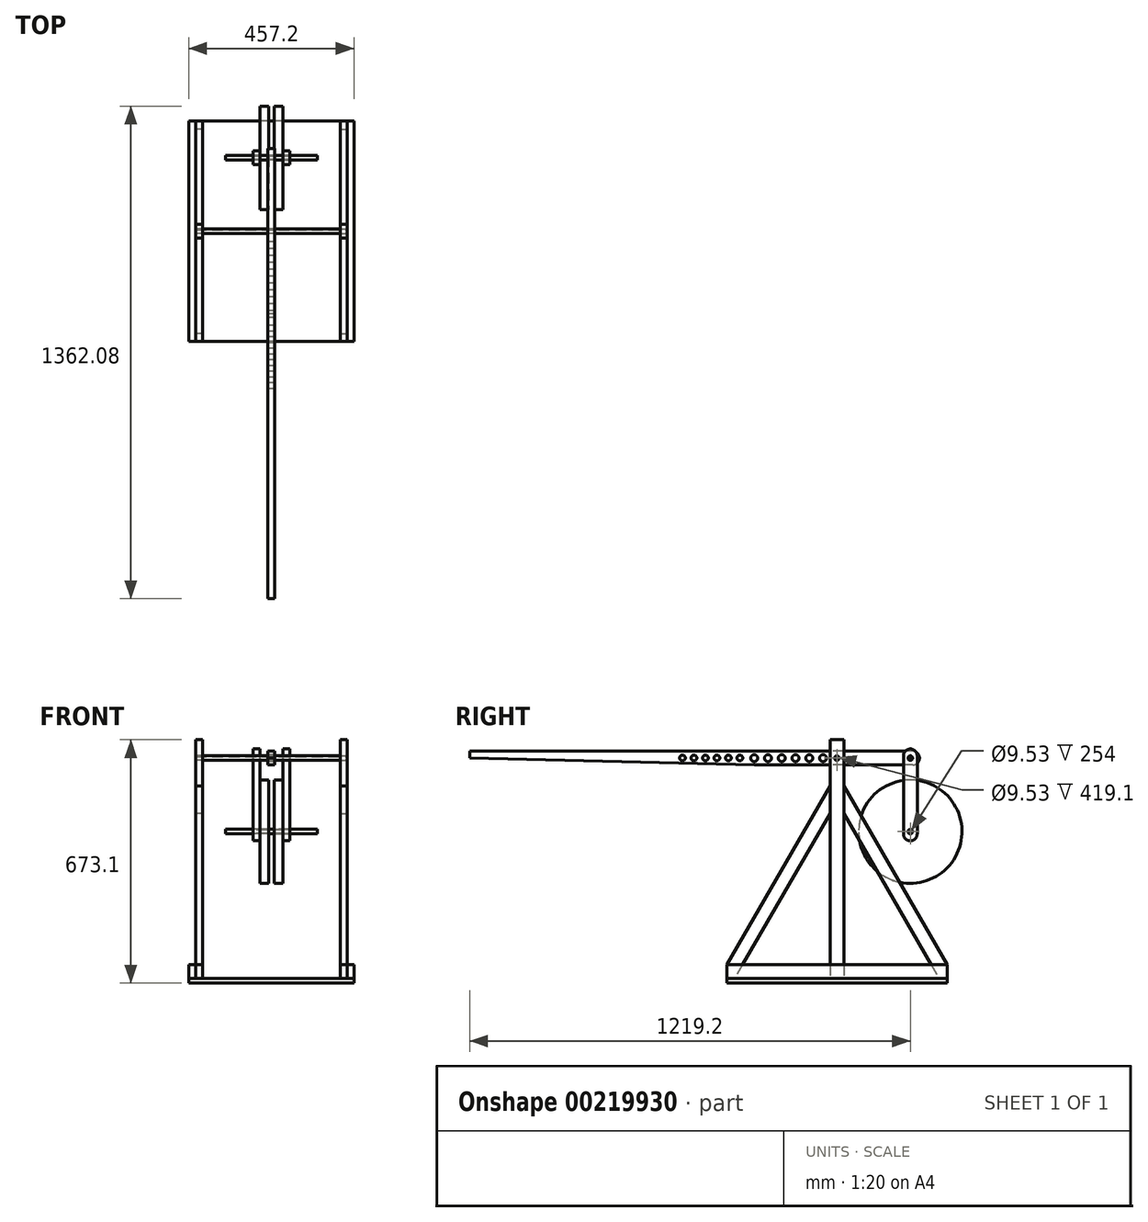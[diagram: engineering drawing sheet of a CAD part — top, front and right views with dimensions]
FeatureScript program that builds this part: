
annotation { "Feature Type Name" : "Feature", "Feature Type Description" : "" }
export const myFeature = defineFeature(function(context is Context, id is Id, definition is map)
    precondition{}
    {
        {
            var Q0;
            Q0=qCreatedBy(makeId("Top.planeOp"),FACE);
            var sketch = newSketch(context, id + "F0", { "sketchPlane" : qUnion([Q0])});
            skLineSegment(sketch, "E0.bottom", {"start": v(-228.6, -304.8) * mm, "end": v(228.6, -304.8) * mm, "construction": true});
            skLineSegment(sketch, "E0.top", {"start": v(-228.6, 304.8) * mm, "end": v(228.6, 304.8) * mm, "construction": true});
            skLineSegment(sketch, "E0.left", {"start": v(-228.6, -304.8) * mm, "end": v(-228.6, 304.8) * mm, "construction": true});
            skLineSegment(sketch, "E0.right", {"start": v(228.6, -304.8) * mm, "end": v(228.6, 304.8) * mm, "construction": true});
            skPoint(sketch, "E0.middle", {"position": v(0, 0) * mm});
            skLineSegment(sketch, "E1.bottom", {"start": v(-228.6, 304.8) * mm, "end": v(-209.55, 304.8) * mm});
            skLineSegment(sketch, "E1.top", {"start": v(-228.6, -304.8) * mm, "end": v(-209.55, -304.8) * mm});
            skLineSegment(sketch, "E1.left", {"start": v(-228.6, 304.8) * mm, "end": v(-228.6, -304.8) * mm});
            skLineSegment(sketch, "E1.right", {"start": v(-209.55, 304.8) * mm, "end": v(-209.55, -304.8) * mm});
            skLineSegment(sketch, "E2.MirrorCS", {"start": v(228.6, -304.8) * mm, "end": v(209.55, -304.8) * mm});
            skLineSegment(sketch, "E3.MirrorCS", {"start": v(228.6, 304.8) * mm, "end": v(228.6, -304.8) * mm});
            skLineSegment(sketch, "E4.MirrorCS", {"start": v(209.55, 304.8) * mm, "end": v(209.55, -304.8) * mm});
            skLineSegment(sketch, "E5.MirrorCS", {"start": v(228.6, 304.8) * mm, "end": v(209.55, 304.8) * mm});
            skSolve(sketch);
        }
        {
            var Q0;
            Q0=makeQuery(id+"F0.imprint","IMPRINT",FACE,{"disambiguationData":[TD([[makeQuery(id+"F0.imprint","IMPRINT",EDGE,{"derivedFrom":sQuery(id+"F0.wireOp",EDGE,"E1.bottom")}),-1.0]])]});
            var Q1;
            Q1=makeQuery(id+"F0.imprint","IMPRINT",FACE,{"disambiguationData":[TD([[makeQuery(id+"F0.imprint","IMPRINT",EDGE,{"derivedFrom":sQuery(id+"F0.wireOp",EDGE,"E2.MirrorCS")}),-1.0]])]});
            extrude(context, id + "F1", {"entities" : qUnion([Q0, Q1]), "depth" : 38.1 * mm});
        }
        {
            var Q0;
            Q0=makeQuery(id+"F1.opExtrude","SWEPT_FACE",FACE,{"disambiguationData":[OSD([sQuery(id+"F0.wireOp",EDGE,"E1.right")])]});
            var sketch = newSketch(context, id + "F2", { "sketchPlane" : qUnion([Q0])});
            skLineSegment(sketch, "E6", {"start": v(-304.8, 0) * mm, "end": v(-304.8, 38.1) * mm});
            skLineSegment(sketch, "E7", {"start": v(-304.8, 38.1) * mm, "end": v(-19.05, 533.03) * mm});
            skLineSegment(sketch, "E8", {"start": v(-19.05, 456.83) * mm, "end": v(-19.05, 533.03) * mm});
            skLineSegment(sketch, "E9", {"start": v(-19.05, 456.83) * mm, "end": v(-282.8, 0) * mm});
            skLineSegment(sketch, "E10", {"start": v(-282.8, 0) * mm, "end": v(-304.8, 0) * mm});
            skLineSegment(sketch, "E11.bottom", {"start": v(-19.05, 660.4) * mm, "end": v(19.05, 660.4) * mm});
            skLineSegment(sketch, "E11.top", {"start": v(-19.05, 0) * mm, "end": v(19.05, 0) * mm});
            skLineSegment(sketch, "E11.left", {"start": v(-19.05, 660.4) * mm, "end": v(-19.05, 0) * mm});
            skLineSegment(sketch, "E11.right", {"start": v(19.05, 660.4) * mm, "end": v(19.05, 0) * mm});
            skLineSegment(sketch, "E12.MirrorCS", {"start": v(304.8, 0) * mm, "end": v(304.8, 38.1) * mm});
            skLineSegment(sketch, "E13.MirrorCS", {"start": v(282.8, 0) * mm, "end": v(304.8, 0) * mm});
            skLineSegment(sketch, "E14.MirrorCS", {"start": v(19.05, 456.83) * mm, "end": v(282.8, 0) * mm});
            skLineSegment(sketch, "E15.MirrorCS", {"start": v(304.8, 38.1) * mm, "end": v(19.05, 533.03) * mm});
            skLineSegment(sketch, "E16.MirrorCS", {"start": v(19.05, 456.83) * mm, "end": v(19.05, 533.03) * mm});
            skCircle(sketch, "E17", {"center": v(0, 609.6) * mm, "radius": 6.35 * mm});
            skSolve(sketch);
        }
        {
            var Q0;
            {var subQ0=sQuery(id+"F2.wireOp",EDGE,"E7");Q0=makeQuery(id+"F2.imprint","IMPRINT",FACE,{"disambiguationData":[TD([[makeQuery(id+"F2.imprint","IMPRINT",EDGE,{"derivedFrom":subQ0}),-1.0]])]});}
            var Q1;
            {var subQ0=sQuery(id+"F2.wireOp",EDGE,"E6");Q1=makeQuery(id+"F2.imprint","IMPRINT",FACE,{"disambiguationData":[TD([[makeQuery(id+"F2.imprint","IMPRINT",EDGE,{"derivedFrom":subQ0}),1.0]])]});}
            var Q2;
            {var subQ4=sQuery(id+"F2.wireOp",EDGE,"E15.MirrorCS");Q2=makeQuery(id+"F2.imprint","IMPRINT",FACE,{"disambiguationData":[TD([[makeQuery(id+"F2.imprint","IMPRINT",EDGE,{"derivedFrom":subQ4}),1.0]])]});}
            var Q3;
            {var subQ0=sQuery(id+"F2.wireOp",EDGE,"E12.MirrorCS");Q3=makeQuery(id+"F2.imprint","IMPRINT",FACE,{"disambiguationData":[TD([[makeQuery(id+"F2.imprint","IMPRINT",EDGE,{"derivedFrom":subQ0}),-1.0]])]});}
            extrude(context, id + "F3", {"entities" : qUnion([Q0, Q1, Q2, Q3]), "depth" : 19.05 * mm});
        }
        {
            var Q0;
            {var subQ5=sQuery(id+"F2.wireOp",EDGE,"E11.bottom");Q0=makeQuery(id+"F2.imprint","IMPRINT",FACE,{"disambiguationData":[TD([[makeQuery(id+"F2.imprint","IMPRINT",EDGE,{"derivedFrom":subQ5}),-1.0]])]});}
            var Q1;
            {var subQ0=sQuery(id+"F2.wireOp",EDGE,"E11.top");Q1=makeQuery(id+"F2.imprint","IMPRINT",FACE,{"disambiguationData":[TD([[makeQuery(id+"F2.imprint","IMPRINT",EDGE,{"derivedFrom":subQ0}),-1.0]])]});}
            extrude(context, id + "F4", {"entities" : qUnion([Q0, Q1]), "depth" : 19.05 * mm});
        }
        {
            var Q0;
            Q0=makeQuery(id+"F3.opExtrude","SWEPT_BODY",BODY,{"disambiguationData":[OSD([sQuery(id+"F2.wireOp",EDGE,"E12.MirrorCS"),sQuery(id+"F2.wireOp",EDGE,"E13.MirrorCS"),sQuery(id+"F2.wireOp",EDGE,"E14.MirrorCS"),sQuery(id+"F2.wireOp",EDGE,"E15.MirrorCS"),sQuery(id+"F2.wireOp",EDGE,"E16.MirrorCS")])]});
            var Q1;
            Q1=qCreatedBy(makeId("Right.planeOp"),FACE);
            mirror(context, id + "F5", {"entities" : qUnion([Q0]), "mirrorPlane" : qUnion([Q1])});
        }
        {
            var Q0;
            Q0=makeQuery(id+"F4.opExtrude","SWEPT_BODY",BODY,{"disambiguationData":[OSD([sQuery(id+"F2.wireOp",EDGE,"E11.bottom"),sQuery(id+"F2.wireOp",EDGE,"E11.top"),sQuery(id+"F2.wireOp",EDGE,"E11.left"),sQuery(id+"F2.wireOp",EDGE,"E11.right"),sQuery(id+"F2.wireOp",EDGE,"E16.MirrorCS"),sQuery(id+"F2.wireOp",EDGE,"E17")])]});
            var Q1;
            Q1=qCreatedBy(makeId("Right.planeOp"),FACE);
            mirror(context, id + "F6", {"entities" : qUnion([Q0]), "mirrorPlane" : qUnion([Q1])});
        }
        {
            var Q0;
            Q0=makeQuery(id+"F3.opExtrude","SWEPT_BODY",BODY,{"disambiguationData":[OSD([sQuery(id+"F2.wireOp",EDGE,"E6"),sQuery(id+"F2.wireOp",EDGE,"E7"),sQuery(id+"F2.wireOp",EDGE,"E9"),sQuery(id+"F2.wireOp",EDGE,"E10"),sQuery(id+"F2.wireOp",EDGE,"E11.left")])]});
            var Q1;
            Q1=qCreatedBy(makeId("Right.planeOp"),FACE);
            mirror(context, id + "F7", {"entities" : qUnion([Q0]), "mirrorPlane" : qUnion([Q1])});
        }
        {
            var Q0;
            Q0=makeQuery(id+"F6.opPattern","COPY",FACE,{"derivedFrom":makeQuery(id+"F4.opExtrude","CAP_FACE",FACE,{"disambiguationData":[OSD([sQuery(id+"F2.wireOp",EDGE,"E11.bottom"),sQuery(id+"F2.wireOp",EDGE,"E11.top"),sQuery(id+"F2.wireOp",EDGE,"E11.left"),sQuery(id+"F2.wireOp",EDGE,"E11.right"),sQuery(id+"F2.wireOp",EDGE,"E16.MirrorCS"),sQuery(id+"F2.wireOp",EDGE,"E17")])],"isStart":true}),"instanceName":"1"});
            var sketch = newSketch(context, id + "F8", { "sketchPlane" : qUnion([Q0])});
            skCircle(sketch, "E18", {"center": v(0, 609.6) * mm, "radius": 4.76 * mm});
            skCircle(sketch, "E19.0", {"center": v(0, 609.6) * mm, "radius": 6.35 * mm});
            skSolve(sketch);
        }
        {
            var Q0;
            Q0=makeQuery(id+"F8.imprint","IMPRINT",FACE,{"disambiguationData":[TD([[makeQuery(id+"F8.imprint","IMPRINT",EDGE,{"derivedFrom":sQuery(id+"F8.wireOp",EDGE,"E18")}),-1.0]])]});
            var Q1;
            Q1=makeQuery(id+"F4.opExtrude","CAP_FACE",FACE,{"disambiguationData":[OSD([sQuery(id+"F2.wireOp",EDGE,"E11.bottom"),sQuery(id+"F2.wireOp",EDGE,"E11.top"),sQuery(id+"F2.wireOp",EDGE,"E11.left"),sQuery(id+"F2.wireOp",EDGE,"E11.right"),sQuery(id+"F2.wireOp",EDGE,"E16.MirrorCS"),sQuery(id+"F2.wireOp",EDGE,"E17")])],"isStart":true});
            extrude(context, id + "F9", {"entities" : qUnion([Q0]), "endBound" : BoundingType.UP_TO_SURFACE, "oppositeDirection" : true, "endBoundEntityFace" : qUnion([Q1]), "depth" : 372.62 * mm});
        }
        {
            var Q0;
            Q0=qCreatedBy(makeId("Top.planeOp"),FACE);
            var sketch = newSketch(context, id + "F10", { "sketchPlane" : qUnion([Q0])});
            skLineSegment(sketch, "E20.bottom", {"start": v(228.6, 304.8) * mm, "end": v(-228.6, 304.8) * mm});
            skLineSegment(sketch, "E20.top", {"start": v(228.6, -304.8) * mm, "end": v(-228.6, -304.8) * mm});
            skLineSegment(sketch, "E20.left", {"start": v(228.6, 304.8) * mm, "end": v(228.6, -304.8) * mm});
            skLineSegment(sketch, "E20.right", {"start": v(-228.6, 304.8) * mm, "end": v(-228.6, -304.8) * mm});
            skPoint(sketch, "E20.middle", {"position": v(0, 0) * mm});
            skSolve(sketch);
        }
        {
            var Q0;
            Q0=makeQuery(id+"F10.imprint","IMPRINT",FACE,{"disambiguationData":[TD([[makeQuery(id+"F10.imprint","IMPRINT",EDGE,{"derivedFrom":sQuery(id+"F10.wireOp",EDGE,"E20.bottom")}),1.0]])]});
            extrude(context, id + "F11", {"entities" : qUnion([Q0]), "oppositeDirection" : true, "depth" : 12.7 * mm});
        }
        {
            var Q0;
            Q0=qCreatedBy(makeId("Right.planeOp"),FACE);
            var sketch = newSketch(context, id + "F12", { "sketchPlane" : qUnion([Q0])});
            skCircle(sketch, "E21.0", {"center": v(0, 609.6) * mm, "radius": 6.35 * mm});
            skLineSegment(sketch, "E22.bottom", {"start": v(228.6, 628.65) * mm, "end": v(-228.6, 628.65) * mm});
            skLineSegment(sketch, "E22.top", {"start": v(228.6, 590.55) * mm, "end": v(-228.6, 590.55) * mm});
            skLineSegment(sketch, "E22.left", {"start": v(228.6, 628.65) * mm, "end": v(228.6, 590.55) * mm});
            skLineSegment(sketch, "E22.right", {"start": v(-228.6, 628.65) * mm, "end": v(-228.6, 590.55) * mm});
            skCircle(sketch, "E23", {"center": v(203.2, 609.6) * mm, "radius": 6.35 * mm});
            skLineSegment(sketch, "E24", {"start": v(-228.6, 628.65) * mm, "end": v(-1016, 628.65) * mm});
            skLineSegment(sketch, "E25", {"start": v(-1016, 628.65) * mm, "end": v(-1016, 609.6) * mm});
            skLineSegment(sketch, "E26", {"start": v(-1016, 609.6) * mm, "end": v(-228.6, 590.55) * mm});
            skCircle(sketch, "E27", {"center": v(-38.1, 609.6) * mm, "radius": 9.53 * mm});
            skCircle(sketch, "E28.1.0.0", {"center": v(-76.2, 609.6) * mm, "radius": 9.53 * mm});
            skCircle(sketch, "E28.2.0.0", {"center": v(-114.3, 609.6) * mm, "radius": 9.53 * mm});
            skCircle(sketch, "E28.3.0.0", {"center": v(-152.4, 609.6) * mm, "radius": 9.53 * mm});
            skCircle(sketch, "E28.4.0.0", {"center": v(-190.5, 609.6) * mm, "radius": 9.53 * mm});
            skCircle(sketch, "E28.5.0.0", {"center": v(-228.6, 609.6) * mm, "radius": 9.53 * mm});
            skLineSegment(sketch, "E28.direction1", {"start": v(-38.1, 609.6) * mm, "end": v(-76.2, 609.6) * mm, "construction": true});
            skLineSegment(sketch, "E29", {"start": v(-1016, 619.12) * mm, "end": v(-228.6, 609.6) * mm, "construction": true});
            skCircle(sketch, "E30", {"center": v(-268.28, 610.08) * mm, "radius": 7.94 * mm});
            skCircle(sketch, "E31.1.0.0", {"center": v(-300.03, 610.08) * mm, "radius": 7.94 * mm});
            skCircle(sketch, "E31.2.0.0", {"center": v(-331.78, 610.08) * mm, "radius": 7.94 * mm});
            skCircle(sketch, "E31.3.0.0", {"center": v(-363.53, 610.08) * mm, "radius": 7.94 * mm});
            skCircle(sketch, "E31.4.0.0", {"center": v(-395.28, 610.08) * mm, "radius": 7.94 * mm});
            skCircle(sketch, "E31.5.0.0", {"center": v(-427.03, 610.08) * mm, "radius": 7.94 * mm});
            skLineSegment(sketch, "E31.direction1", {"start": v(-268.28, 610.08) * mm, "end": v(-300.03, 610.08) * mm, "construction": true});
            skSolve(sketch);
        }
        {
            var Q0;
            {var subQ5=sQuery(id+"F12.wireOp",EDGE,"E24");Q0=makeQuery(id+"F12.imprint","IMPRINT",FACE,{"disambiguationData":[TD([[makeQuery(id+"F12.imprint","IMPRINT",EDGE,{"derivedFrom":subQ5}),1.0]])]});}
            var Q1;
            Q1=makeQuery(id+"F12.imprint","IMPRINT",FACE,{"disambiguationData":[TD([[makeQuery(id+"F12.imprint","IMPRINT",EDGE,{"derivedFrom":sQuery(id+"F12.wireOp",EDGE,"E21.0")}),-1.0]])]});
            extrude(context, id + "F13", {"entities" : qUnion([Q0, Q1]), "endBound" : BoundingType.SYMMETRIC, "depth" : 19.05 * mm});
        }
        {
            var Q0;
            Q0=qCreatedBy(makeId("Right.planeOp"),FACE);
            var sketch = newSketch(context, id + "F14", { "sketchPlane" : qUnion([Q0])});
            skCircle(sketch, "E32.0", {"center": v(203.2, 609.6) * mm, "radius": 6.35 * mm});
            skCircle(sketch, "E33.0", {"center": v(203.2, 609.6) * mm, "radius": 4.76 * mm});
            skSolve(sketch);
        }
        {
            var Q0;
            Q0=makeQuery(id+"F14.imprint","IMPRINT",FACE,{"disambiguationData":[TD([[makeQuery(id+"F14.imprint","IMPRINT",EDGE,{"derivedFrom":sQuery(id+"F14.wireOp",EDGE,"E32.0")}),1.0]])]});
            extrude(context, id + "F15", {"entities" : qUnion([Q0]), "endBound" : BoundingType.SYMMETRIC, "depth" : 101.6 * mm});
        }
        {
            var Q0;
            Q0=makeQuery(id+"F15.opExtrude","CAP_FACE",FACE,{"disambiguationData":[OSD([sQuery(id+"F14.wireOp",EDGE,"E32.0"),sQuery(id+"F14.wireOp",EDGE,"E33.0")])],"isStart":false});
            var sketch = newSketch(context, id + "F16", { "sketchPlane" : qUnion([Q0])});
            skLineSegment(sketch, "E34.bottom", {"start": v(203.2, 635) * mm, "end": v(203.2, 635) * mm});
            skLineSegment(sketch, "E34.top", {"start": v(203.2, 381) * mm, "end": v(203.2, 381) * mm});
            skLineSegment(sketch, "E34.left", {"start": v(222.25, 615.95) * mm, "end": v(222.25, 400.05) * mm});
            skLineSegment(sketch, "E34.right", {"start": v(184.15, 615.95) * mm, "end": v(184.15, 400.05) * mm});
            skPoint(sketch, "E34.middle", {"position": v(203.2, 609.6) * mm});
            skCircle(sketch, "E35", {"center": v(203.2, 406.4) * mm, "radius": 6.35 * mm});
            skPoint(sketch, "E36.visualSharp", {"position": v(184.15, 635) * mm});
            skArc(sketch, "E36.filletArc", {"start": v(203.2, 635) * mm, "mid": v(189.73, 629.42) * mm, "end": v(184.15, 615.95) * mm});
            skPoint(sketch, "E37.visualSharp", {"position": v(222.25, 635) * mm});
            skArc(sketch, "E37.filletArc", {"start": v(222.25, 615.95) * mm, "mid": v(216.67, 629.42) * mm, "end": v(203.2, 635) * mm});
            skPoint(sketch, "E38.visualSharp", {"position": v(222.25, 381) * mm});
            skArc(sketch, "E38.filletArc", {"start": v(203.2, 381) * mm, "mid": v(216.67, 386.58) * mm, "end": v(222.25, 400.05) * mm});
            skPoint(sketch, "E39.visualSharp", {"position": v(184.15, 381) * mm});
            skArc(sketch, "E39.filletArc", {"start": v(184.15, 400.05) * mm, "mid": v(189.73, 386.58) * mm, "end": v(203.2, 381) * mm});
            skLineSegment(sketch, "E40", {"start": v(203.2, 609.6) * mm, "end": v(203.2, 406.4) * mm, "construction": true});
            skSolve(sketch);
        }
        {
            var Q0;
            Q0=makeQuery(id+"F16.imprint","IMPRINT",FACE,{"disambiguationData":[TD([[makeQuery(id+"F16.imprint","IMPRINT",EDGE,{"derivedFrom":sQuery(id+"F16.wireOp",EDGE,"E34.left")}),-1.0]])]});
            extrude(context, id + "F17", {"entities" : qUnion([Q0]), "oppositeDirection" : true, "depth" : 19.05 * mm});
        }
        {
            var Q0;
            Q0=makeQuery(id+"F13.opExtrude","SWEPT_EDGE",EDGE,{"disambiguationData":[OSD([sQuery(id+"F12.wireOp",EDGE,"E22.bottom"),sQuery(id+"F12.wireOp",EDGE,"E22.left")])]});
            var Q1;
            Q1=makeQuery(id+"F13.opExtrude","SWEPT_EDGE",EDGE,{"disambiguationData":[OSD([sQuery(id+"F12.wireOp",EDGE,"E22.top"),sQuery(id+"F12.wireOp",EDGE,"E22.left")])]});
            fillet(context, id + "F18", {"entities" : qUnion([Q0, Q1]), "radius" : 19.05 * mm, "tangentPropagation" : true, "allowEdgeOverflow" : false});
        }
        {
            var Q0;
            Q0=makeQuery(id+"F17.opExtrude","SWEPT_BODY",BODY,{"disambiguationData":[OSD([sQuery(id+"F14.wireOp",EDGE,"E32.0"),sQuery(id+"F16.wireOp",EDGE,"E34.bottom"),sQuery(id+"F16.wireOp",EDGE,"E34.top"),sQuery(id+"F16.wireOp",EDGE,"E34.left"),sQuery(id+"F16.wireOp",EDGE,"E34.right"),sQuery(id+"F16.wireOp",EDGE,"E35"),sQuery(id+"F16.wireOp",EDGE,"E36.filletArc"),sQuery(id+"F16.wireOp",EDGE,"E37.filletArc"),sQuery(id+"F16.wireOp",EDGE,"E38.filletArc"),sQuery(id+"F16.wireOp",EDGE,"E39.filletArc")])]});
            var Q1;
            Q1=qCreatedBy(makeId("Right.planeOp"),FACE);
            mirror(context, id + "F19", {"entities" : qUnion([Q0]), "mirrorPlane" : qUnion([Q1])});
        }
        {
            var Q0;
            Q0=qCreatedBy(makeId("Right.planeOp"),FACE);
            var sketch = newSketch(context, id + "F20", { "sketchPlane" : qUnion([Q0])});
            skCircle(sketch, "E41.0", {"center": v(203.2, 406.4) * mm, "radius": 6.35 * mm});
            skCircle(sketch, "E42.0", {"center": v(203.2, 406.4) * mm, "radius": 4.76 * mm});
            skSolve(sketch);
        }
        {
            var Q0;
            Q0=makeQuery(id+"F20.imprint","IMPRINT",FACE,{"disambiguationData":[TD([[makeQuery(id+"F20.imprint","IMPRINT",EDGE,{"derivedFrom":sQuery(id+"F20.wireOp",EDGE,"E41.0")}),1.0]])]});
            extrude(context, id + "F21", {"entities" : qUnion([Q0]), "endBound" : BoundingType.SYMMETRIC, "depth" : 254 * mm});
        }
        {
            var Q0;
            Q0=makeQuery(id+"F17.opExtrude","CAP_FACE",FACE,{"disambiguationData":[OSD([sQuery(id+"F14.wireOp",EDGE,"E32.0"),sQuery(id+"F16.wireOp",EDGE,"E34.bottom"),sQuery(id+"F16.wireOp",EDGE,"E34.top"),sQuery(id+"F16.wireOp",EDGE,"E34.left"),sQuery(id+"F16.wireOp",EDGE,"E34.right"),sQuery(id+"F16.wireOp",EDGE,"E35"),sQuery(id+"F16.wireOp",EDGE,"E36.filletArc"),sQuery(id+"F16.wireOp",EDGE,"E37.filletArc"),sQuery(id+"F16.wireOp",EDGE,"E38.filletArc"),sQuery(id+"F16.wireOp",EDGE,"E39.filletArc")])],"isStart":false});
            var sketch = newSketch(context, id + "F22", { "sketchPlane" : qUnion([Q0])});
            skCircle(sketch, "E43.0", {"center": v(-203.2, 406.4) * mm, "radius": 6.35 * mm});
            skCircle(sketch, "E44", {"center": v(-203.2, 406.4) * mm, "radius": 142.88 * mm});
            skSolve(sketch);
        }
        {
            var Q0;
            {var subQ5=makeQuery(id+"F17.opExtrude","CAP_EDGE",EDGE,{"disambiguationData":[OSD([sQuery(id+"F16.wireOp",EDGE,"E38.filletArc"),sQuery(id+"F16.wireOp",EDGE,"E39.filletArc")])],"isStart":false});Q0=makeQuery(id+"F22.imprint","IMPRINT",FACE,{"disambiguationData":[TD([[makeQuery(id+"F22.imprint","IMPRINT",EDGE,{"derivedFrom":subQ5}),1.0]])]});}
            var Q1;
            Q1=makeQuery(id+"F22.imprint","IMPRINT",FACE,{"disambiguationData":[TD([[makeQuery(id+"F22.imprint","IMPRINT",EDGE,{"derivedFrom":sQuery(id+"F22.wireOp",EDGE,"E43.0")}),1.0]])]});
            extrude(context, id + "F23", {"entities" : qUnion([Q0, Q1]), "depth" : 24.13 * mm});
        }
        {
            var Q0;
            Q0=makeQuery(id+"F23.opExtrude","SWEPT_BODY",BODY,{"disambiguationData":[OSD([sQuery(id+"F22.wireOp",EDGE,"E43.0"),sQuery(id+"F22.wireOp",EDGE,"E44")])]});
            var Q1;
            Q1=qCreatedBy(makeId("Right.planeOp"),FACE);
            mirror(context, id + "F24", {"entities" : qUnion([Q0]), "mirrorPlane" : qUnion([Q1])});
        }
    });
